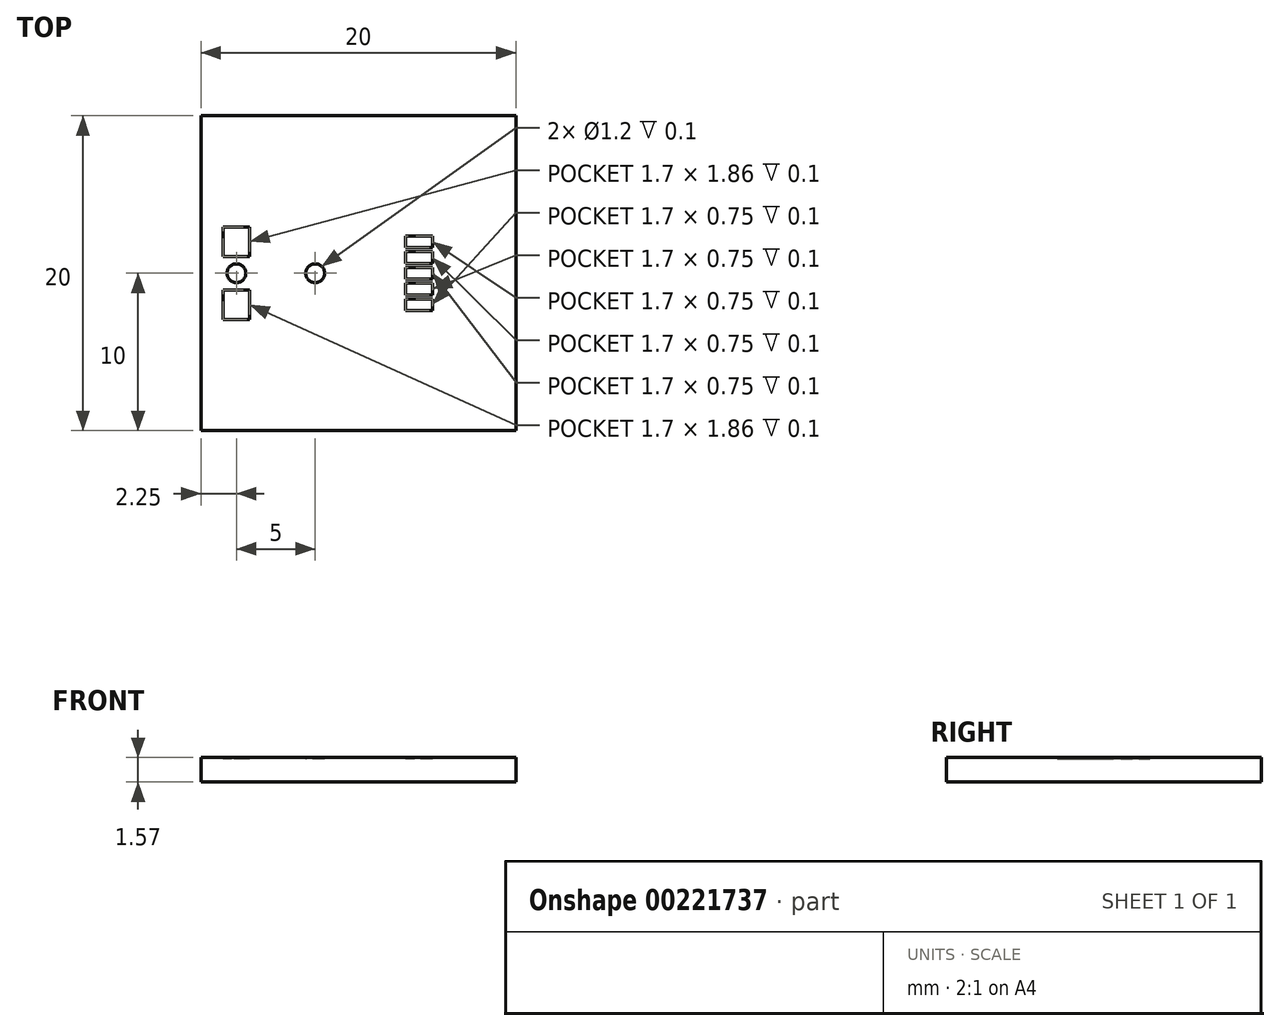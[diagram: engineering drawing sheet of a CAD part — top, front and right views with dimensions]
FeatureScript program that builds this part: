
annotation { "Feature Type Name" : "Feature", "Feature Type Description" : "" }
export const myFeature = defineFeature(function(context is Context, id is Id, definition is map)
    precondition{}
    {
        {
            var Q0;
            Q0=qCreatedBy(makeId("Top.planeOp"),FACE);
            var sketch = newSketch(context, id + "F0", { "sketchPlane" : qUnion([Q0])});
            skLineSegment(sketch, "E0.bottom", {"start": v(10, 10) * mm, "end": v(-10, 10) * mm});
            skLineSegment(sketch, "E0.top", {"start": v(10, -10) * mm, "end": v(-10, -10) * mm});
            skLineSegment(sketch, "E0.left", {"start": v(10, 10) * mm, "end": v(10, -10) * mm});
            skLineSegment(sketch, "E0.right", {"start": v(-10, 10) * mm, "end": v(-10, -10) * mm});
            skPoint(sketch, "E0.middle", {"position": v(0, 0) * mm});
            skSolve(sketch);
        }
        {
            var Q0;
            Q0 = qSketchRegion(id + "F0", true);
            extrude(context, id + "F1", {"entities" : qUnion([Q0]), "depth" : 1.57 * mm});
        }
        {
            var Q0;
            Q0=makeQuery(id+"F1.opExtrude","CAP_FACE",FACE,{"disambiguationData":[OSD([sQuery(id+"F0.wireOp",EDGE,"E0.bottom"),sQuery(id+"F0.wireOp",EDGE,"E0.top"),sQuery(id+"F0.wireOp",EDGE,"E0.left"),sQuery(id+"F0.wireOp",EDGE,"E0.right")])],"isStart":false});
            var sketch = newSketch(context, id + "F2", { "sketchPlane" : qUnion([Q0])});
            skLineSegment(sketch, "E1.bottom", {"start": v(-6.9, 1.07) * mm, "end": v(-8.6, 1.07) * mm});
            skLineSegment(sketch, "E1.top", {"start": v(-6.9, 2.93) * mm, "end": v(-8.6, 2.93) * mm});
            skLineSegment(sketch, "E1.left", {"start": v(-6.9, 1.07) * mm, "end": v(-6.9, 2.93) * mm});
            skLineSegment(sketch, "E1.right", {"start": v(-8.6, 1.07) * mm, "end": v(-8.6, 2.93) * mm});
            skPoint(sketch, "E1.middle", {"position": v(-7.75, 2) * mm});
            skLineSegment(sketch, "E2.bottom", {"start": v(-6.9, -2.93) * mm, "end": v(-8.6, -2.93) * mm});
            skLineSegment(sketch, "E2.top", {"start": v(-6.9, -1.07) * mm, "end": v(-8.6, -1.07) * mm});
            skLineSegment(sketch, "E2.left", {"start": v(-6.9, -2.93) * mm, "end": v(-6.9, -1.07) * mm});
            skLineSegment(sketch, "E2.right", {"start": v(-8.6, -2.93) * mm, "end": v(-8.6, -1.07) * mm});
            skPoint(sketch, "E2.middle", {"position": v(-7.75, -2) * mm});
            skLineSegment(sketch, "E3", {"start": v(0, 0) * mm, "end": v(-10, 0) * mm, "construction": true});
            skLineSegment(sketch, "E4", {"start": v(-7.75, 0) * mm, "end": v(-7.75, -2) * mm, "construction": true});
            skLineSegment(sketch, "E5", {"start": v(-7.75, 2) * mm, "end": v(-7.75, 0) * mm, "construction": true});
            skCircle(sketch, "E6", {"center": v(-7.75, 0) * mm, "radius": 0.6 * mm});
            skCircle(sketch, "E7", {"center": v(-2.75, 0) * mm, "radius": 0.6 * mm});
            skLineSegment(sketch, "E8.bottom", {"start": v(3, 0.37) * mm, "end": v(4.7, 0.37) * mm});
            skLineSegment(sketch, "E8.top", {"start": v(3, -0.38) * mm, "end": v(4.7, -0.38) * mm});
            skLineSegment(sketch, "E8.left", {"start": v(3, 0.38) * mm, "end": v(3, -0.38) * mm});
            skLineSegment(sketch, "E8.right", {"start": v(4.7, 0.38) * mm, "end": v(4.7, -0.38) * mm});
            skLineSegment(sketch, "E9", {"start": v(3, 0) * mm, "end": v(4.7, 0) * mm, "construction": true});
            skLineSegment(sketch, "E10.bottom", {"start": v(4.7, 1.37) * mm, "end": v(3, 1.37) * mm});
            skLineSegment(sketch, "E10.top", {"start": v(4.7, 0.62) * mm, "end": v(3, 0.62) * mm});
            skLineSegment(sketch, "E10.left", {"start": v(4.7, 1.37) * mm, "end": v(4.7, 0.62) * mm});
            skLineSegment(sketch, "E10.right", {"start": v(3, 1.37) * mm, "end": v(3, 0.62) * mm});
            skPoint(sketch, "E10.middle", {"position": v(3.85, 1) * mm});
            skPoint(sketch, "E10.middle.positionSnap0", {"position": v(3.85, 0.37) * mm});
            skPoint(sketch, "E10.centerSnap0", {"position": v(3.85, 0.37) * mm});
            skLineSegment(sketch, "E11.bottom", {"start": v(4.7, 2.38) * mm, "end": v(3, 2.38) * mm});
            skLineSegment(sketch, "E11.top", {"start": v(4.7, 1.62) * mm, "end": v(3, 1.62) * mm});
            skLineSegment(sketch, "E11.left", {"start": v(4.7, 2.38) * mm, "end": v(4.7, 1.62) * mm});
            skLineSegment(sketch, "E11.right", {"start": v(3, 2.38) * mm, "end": v(3, 1.62) * mm});
            skPoint(sketch, "E11.middle", {"position": v(3.85, 2) * mm});
            skLineSegment(sketch, "E12.bottom", {"start": v(4.7, -1.38) * mm, "end": v(3, -1.38) * mm});
            skLineSegment(sketch, "E12.top", {"start": v(4.7, -0.62) * mm, "end": v(3, -0.62) * mm});
            skLineSegment(sketch, "E12.left", {"start": v(4.7, -1.38) * mm, "end": v(4.7, -0.62) * mm});
            skLineSegment(sketch, "E12.right", {"start": v(3, -1.38) * mm, "end": v(3, -0.62) * mm});
            skPoint(sketch, "E12.middle", {"position": v(3.85, -1) * mm});
            skLineSegment(sketch, "E13.bottom", {"start": v(4.7, -2.38) * mm, "end": v(3, -2.38) * mm});
            skLineSegment(sketch, "E13.top", {"start": v(4.7, -1.62) * mm, "end": v(3, -1.62) * mm});
            skLineSegment(sketch, "E13.left", {"start": v(4.7, -2.38) * mm, "end": v(4.7, -1.62) * mm});
            skLineSegment(sketch, "E13.right", {"start": v(3, -2.38) * mm, "end": v(3, -1.62) * mm});
            skPoint(sketch, "E13.middle", {"position": v(3.85, -2) * mm});
            skSolve(sketch);
        }
        {
            var Q0;
            Q0 = qSketchRegion(id + "F2", true);
            extrude(context, id + "F3", {"entities" : qUnion([Q0]), "operationType" : NewBodyOperationType.REMOVE, "oppositeDirection" : true, "depth" : .1 * mm});
        }
    });
